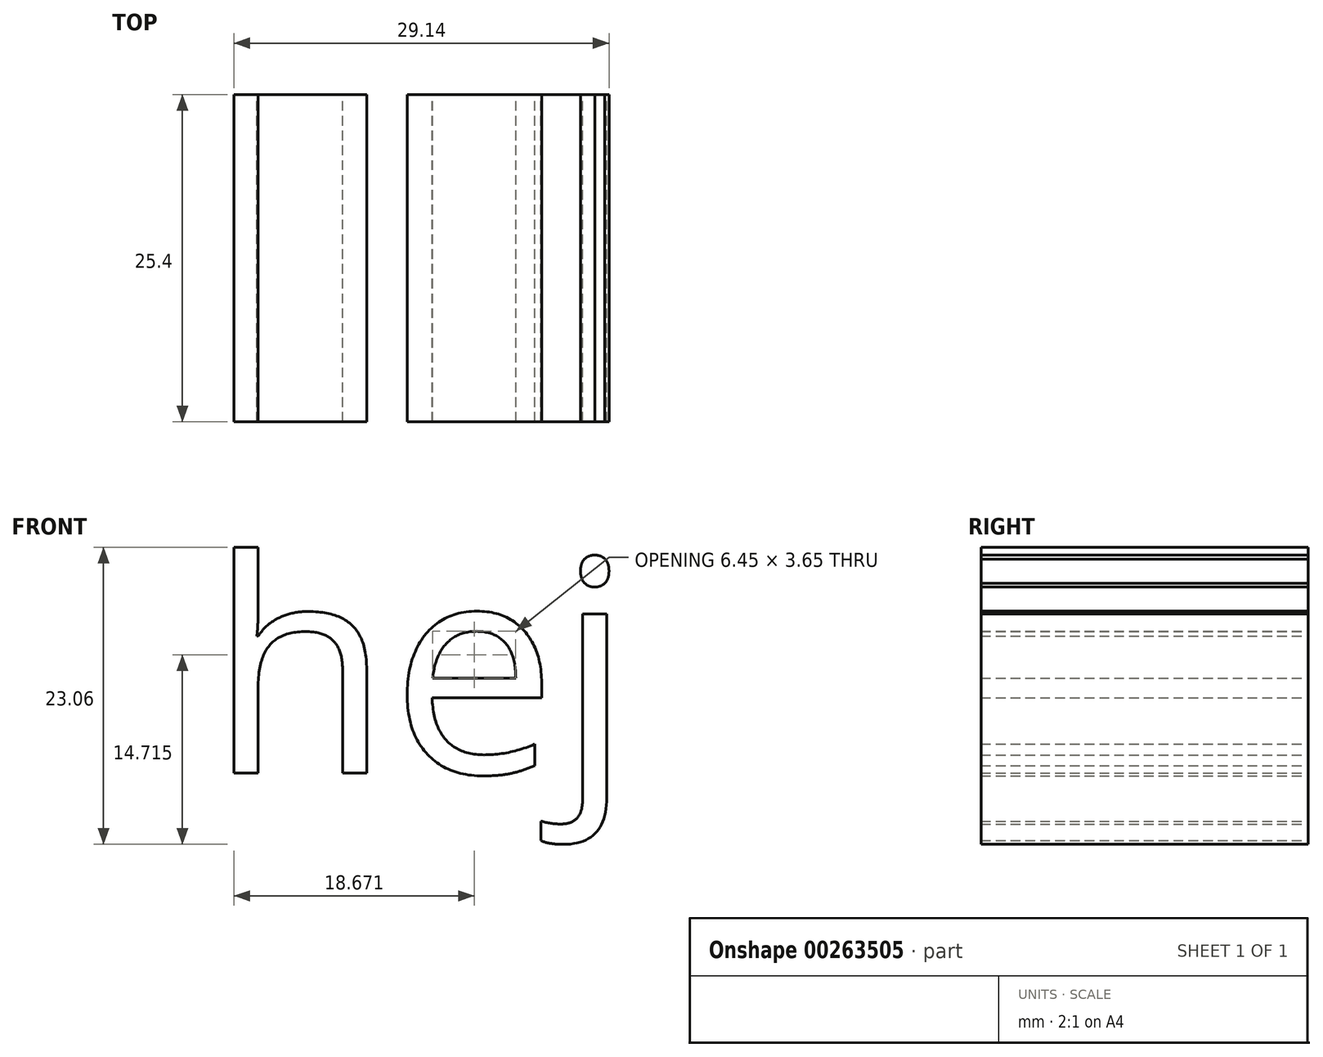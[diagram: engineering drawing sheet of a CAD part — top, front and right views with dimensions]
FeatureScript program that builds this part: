
annotation { "Feature Type Name" : "Feature", "Feature Type Description" : "" }
export const myFeature = defineFeature(function(context is Context, id is Id, definition is map)
    precondition{}
    {
        {
            var Q0;
            Q0=qCreatedBy(makeId("Front.planeOp"),FACE);
            var sketch = newSketch(context, id + "F0", { "sketchPlane" : qUnion([Q0])});
            skText(sketch, "E0", { "text": "hej", "fontName": "OpenSans-Regular.ttf"});
            const initialGuessF0  = {"E0": [-0.03262, -0.04999, 1, 0, 0.0166]};
            skSetInitialGuess(sketch, initialGuessF0);
            skSolve(sketch);
        }
        {
            var Q0;
            Q0 = qSketchRegion(id + "F0", true);
            extrude(context, id + "F1", {"entities" : qUnion([Q0]), "depth" : 25.4 * mm});
        }
    });
